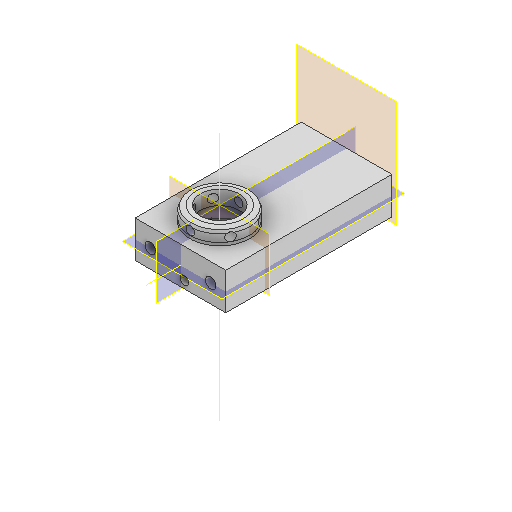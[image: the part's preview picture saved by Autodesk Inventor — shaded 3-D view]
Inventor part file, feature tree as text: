
AUTODESK INVENTOR PART (.ipt)
format: ipt  version: 2022 (Build 260153000, 153)  size: 346,112 bytes
history: native  units: mm
features: other x10, reference x7, sketch x6, plane x4, extrude x4, revolve x2, chamfer x2, pattern_circular x2, projected_geometry x1
ambient origin geometry x8: Origin, YZ Plane, XZ Plane, XY Plane, X Axis, Y Axis, Z Axis, Center Point
bodies: Volumenkörper1 (feature_tree)
feature tree (38):
  plane  "Arbeitsebene1"
  extrude  "Extrusion1"  Depth=3.5mm
  extrude  "Extrusion2"  Depth=20.0mm
  plane  "Arbeitsebene2"
  plane  "Arbeitsebene3"
  other  "Spirale1"
  revolve  "Umdrehung1"
  chamfer  "Fase2"  Distance=60.0mm
  chamfer  "Fase3"  Distance=3.490659mm
  other  "Arbeitsachse2"
  pattern_circular  "Runde Anordnung4"  Angle=45.0deg  [1 undecoded]
  revolve  "Umdrehung2"
  extrude  "Extrusion4"  Depth=10.0mm TaperAngle=45.0deg
  pattern_circular  "Runde Anordnung5"  [2 undecoded]
  extrude  "Extrusion5"  Depth=10.0mm
  sketch  "Skizze1"  dims[d0=3.5mm d1=3.5mm]
  reference  "Referenz1"
  sketch  "Skizze2"  dims[d2=55.0mm d3=0.0mm d4=20.0mm]
  reference  "Referenz2"
  other  "Arbeitsachse1"
  other  "Arbeitspunkt1"
  sketch  "Skizze4"  dims[d5=50.0mm d6=60.0mm d7=0.0mm]
  plane  "Arbeitsebene4"
  sketch  "Skizze6"  dims[d11=2.0mm]
  reference  "Referenz3"
  reference  "Referenz4"
  reference  "Referenz5"
  reference  "Referenz6"
  sketch  "Skizze7"  dims[d12=3.2mm]
  reference  "Referenz7"
  sketch  "Skizze8"  dims[d14=6.0mm d15=10.0mm d16=1.5mm d17=0.0mm d18=90.0deg d19=90.0deg d20=0.0mm d21=0.0mm d22=3.490659mm d23=0.5mm d24=2.0mm d25=45.0deg d31=0.5mm d32=2.0mm d33=45.0deg d34=0.0mm d35=0.1mm d36=6.1mm d43=30.0mm d44=360.0deg d49=90.0deg d50=0.0mm d51=0.0mm d52=60.0mm d53=360.0deg d55=10.0mm d56=2.8mm d57=10.0mm d58=0.0mm]
  projected_geometry  "Projizierte Kontur1"
  other  "Assembly_Cube_Z-Stage_NEMA11_universal.iam"
  other  "00_Linear_Stage_NEMA11_25mm_china:1"
  other  "Carriage:1"
  other  "Nema11:1"
  other  "30_Linear_Stage_NEMA11_baseholder_bayonetmount_objective_v0:3"
  other  "Baugruppe2"
note: 3 required parameter values undecoded (feature->parameter linkage not recoverable at this tier; creation-order binding heuristic only, values carry confidence <= 0.55)
